# Revit family: Basin-American_Standard-Reliant-0614200.020
name_source: partatom
category: Plumbing Fixtures
units: mm (PartAtom-declared; Revit-internal decimal feet)

## family parameters
Always vertical = No
Cut with Voids When Loaded = Yes
OmniClass Number = 23.45.05.14.14
OmniClass Title = Sinks/Lavatories
Part Type = Normal
Room Calculation Point = No
Round Connector Dimension = Use Radius
Shared = Yes
Work Plane-Based = Yes

## types (1)
- 0614200.020
    ADA Compliant = Yes
    Assembly Code = D2010310
    Basin Shape = Rectangular
    CW Connection = Yes
    CWFU = 1.5
    Cold Water Connection Diameter = 3/8"
    Cold Water Connection Height = 22 1/2"
    Cold Water Connection Radius = 3/16"
    Default Elevation = 34"
    Description = Reliant® Rectangular Under Counter Sink
    Finish = Vitreous China-American Standard-020-White
    HW Connection = Yes
    HWFU = 1.5
    Height = 8 1/2"
    Hot Water Connection Diameter = 3/8"
    Hot Water Connection Height = 22 1/2"
    Hot Water Connection Radius = 3/16"
    IAPMO Compliance = Meets or Exceeds the Following Specifications -  ASMEA112.19.2M for Vitreous China Fixtures  and CAN/CSA B45 series
    Installation Type = Undermount
    Length = 13 3/4"
    Manufacturer = American Standard
    Material = Vitreous China-American Standard-020-White
    Model = 0614200.020
    Price = Prices may vary. Please consult Manufacturer Rep for most up-to-date price list.
    Product Page URL = https://www.americanstandard-us.com
    Revised Date = 04/21/2022
    URL = http://www.americanstandard-us.com
    Vent Connection = No
    WFU = 2
    Waste Connection = Yes
    Waste Connection Diameter = 1 1/4"
    Waste Connection Height = 20 1/4"
    Waste Connection Radius = 5/8"
    Width = 19 3/4"

## geometry (parser evidence)
native form markers: Sweep x2
no freeform markers — native parametric forms only
